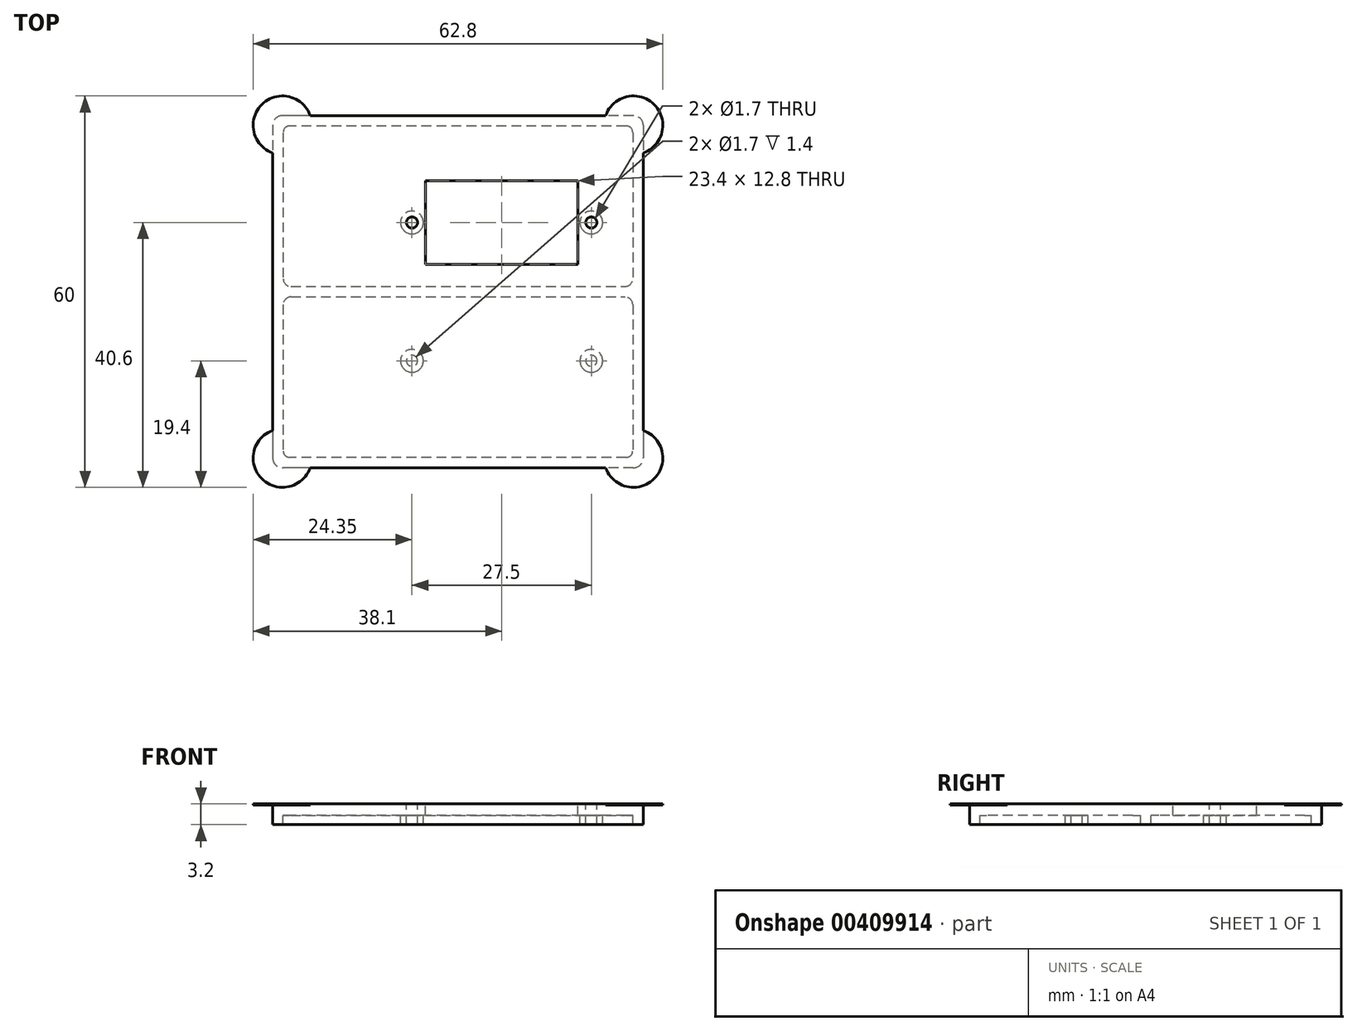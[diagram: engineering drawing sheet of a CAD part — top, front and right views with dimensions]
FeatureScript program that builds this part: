
annotation { "Feature Type Name" : "Feature", "Feature Type Description" : "" }
export const myFeature = defineFeature(function(context is Context, id is Id, definition is map)
    precondition{}
    {
        {
            var Q0;
            Q0=qCreatedBy(makeId("Top.planeOp"),FACE);
            var sketch = newSketch(context, id + "F0", { "sketchPlane" : qUnion([Q0])});
            skLineSegment(sketch, "E0.bottom", {"start": v(28.4, 27) * mm, "end": v(-28.4, 27) * mm});
            skLineSegment(sketch, "E0.top", {"start": v(28.4, -27) * mm, "end": v(-28.4, -27) * mm});
            skLineSegment(sketch, "E0.left", {"start": v(28.4, 27) * mm, "end": v(28.4, -27) * mm});
            skLineSegment(sketch, "E0.right", {"start": v(-28.4, 27) * mm, "end": v(-28.4, -27) * mm});
            skPoint(sketch, "E0.middle", {"position": v(0, 0) * mm});
            skCircle(sketch, "E1", {"center": v(-17.5, 14) * mm, "radius": 1.35 * mm, "construction": true});
            skCircle(sketch, "E2", {"center": v(-17.5, -14) * mm, "radius": 1.35 * mm, "construction": true});
            skCircle(sketch, "E3", {"center": v(17.5, 14) * mm, "radius": 1.35 * mm, "construction": true});
            skCircle(sketch, "E4", {"center": v(17.5, -14) * mm, "radius": 1.35 * mm, "construction": true});
            skLineSegment(sketch, "E5.bottom", {"start": v(-17.5, 14) * mm, "end": v(17.5, 14) * mm, "construction": true});
            skLineSegment(sketch, "E5.top", {"start": v(-17.5, -14) * mm, "end": v(17.5, -14) * mm, "construction": true});
            skLineSegment(sketch, "E5.left", {"start": v(-17.5, 14) * mm, "end": v(-17.5, -14) * mm, "construction": true});
            skLineSegment(sketch, "E5.right", {"start": v(17.5, 14) * mm, "end": v(17.5, -14) * mm, "construction": true});
            skLineSegment(sketch, "E6", {"start": v(-17.5, 0) * mm, "end": v(0, 0) * mm, "construction": true});
            skLineSegment(sketch, "E7", {"start": v(0, 14) * mm, "end": v(0, 0) * mm, "construction": true});
            skSolve(sketch);
        }
        {
            var Q0;
            Q0=qSketchRegion(id+"F0",true);
            extrude(context, id + "F1", {"entities" : qUnion([Q0]), "depth" : 1.8 * mm});
        }
        {
            var Q0;
            Q0=makeQuery(id+"F1.opExtrude","CAP_FACE",FACE,{"disambiguationData":[OSD([sQuery(id+"F0.wireOp",EDGE,"E0.bottom"),sQuery(id+"F0.wireOp",EDGE,"E0.top"),sQuery(id+"F0.wireOp",EDGE,"E0.left"),sQuery(id+"F0.wireOp",EDGE,"E0.right")])],"isStart":false});
            var sketch = newSketch(context, id + "F2", { "sketchPlane" : qUnion([Q0])});
            skLineSegment(sketch, "E8.bottom", {"start": v(-5, 4.2) * mm, "end": v(18.4, 4.2) * mm});
            skLineSegment(sketch, "E8.top", {"start": v(-5, 17) * mm, "end": v(18.4, 17) * mm});
            skLineSegment(sketch, "E8.left", {"start": v(-5, 4.2) * mm, "end": v(-5, 17) * mm});
            skLineSegment(sketch, "E8.right", {"start": v(18.4, 4.2) * mm, "end": v(18.4, 17) * mm});
            skCircle(sketch, "E9", {"center": v(-7.05, 10.6) * mm, "radius": 0.85 * mm});
            skPoint(sketch, "E9.centerSnap0", {"position": v(-5, 10.6) * mm});
            skCircle(sketch, "E10", {"center": v(20.45, 10.6) * mm, "radius": 0.85 * mm});
            skPoint(sketch, "E10.centerSnap0", {"position": v(18.4, 10.6) * mm});
            skLineSegment(sketch, "E11", {"start": v(-7.05, 10.6) * mm, "end": v(-5, 10.6) * mm, "construction": true});
            skLineSegment(sketch, "E12", {"start": v(18.4, 10.6) * mm, "end": v(20.45, 10.6) * mm, "construction": true});
            skSolve(sketch);
        }
        {
            var Q0;
            Q0=qSketchRegion(id+"F2",true);
            extrude(context, id + "F3", {"entities" : qUnion([Q0]), "operationType" : NewBodyOperationType.REMOVE, "endBound" : BoundingType.THROUGH_ALL, "oppositeDirection" : true, "depth" : 25 * mm});
        }
        {
            var Q0;
            Q0=makeQuery(id+"F1.opExtrude","SWEPT_EDGE",EDGE,{"disambiguationData":[OSD([sQuery(id+"F0.wireOp",EDGE,"E0.bottom"),sQuery(id+"F0.wireOp",EDGE,"E0.left")])]});
            var Q1;
            Q1=makeQuery(id+"F1.opExtrude","SWEPT_EDGE",EDGE,{"disambiguationData":[OSD([sQuery(id+"F0.wireOp",EDGE,"E0.top"),sQuery(id+"F0.wireOp",EDGE,"E0.left")])]});
            var Q2;
            Q2=makeQuery(id+"F1.opExtrude","SWEPT_EDGE",EDGE,{"disambiguationData":[OSD([sQuery(id+"F0.wireOp",EDGE,"E0.top"),sQuery(id+"F0.wireOp",EDGE,"E0.right")])]});
            var Q3;
            Q3=makeQuery(id+"F1.opExtrude","SWEPT_EDGE",EDGE,{"disambiguationData":[OSD([sQuery(id+"F0.wireOp",EDGE,"E0.bottom"),sQuery(id+"F0.wireOp",EDGE,"E0.right")])]});
            fillet(context, id + "F4", {"entities" : qUnion([Q0, Q1, Q2, Q3]), "radius" : 1.5 * mm, "tangentPropagation" : true, "allowEdgeOverflow" : false});
        }
        {
            var Q0;
            Q0=makeQuery(id+"F1.opExtrude","CAP_FACE",FACE,{"disambiguationData":[OSD([sQuery(id+"F0.wireOp",EDGE,"E0.bottom"),sQuery(id+"F0.wireOp",EDGE,"E0.top"),sQuery(id+"F0.wireOp",EDGE,"E0.left"),sQuery(id+"F0.wireOp",EDGE,"E0.right"),sQuery(id+"F0.wireOp",EDGE,"E1"),sQuery(id+"F0.wireOp",EDGE,"E2"),sQuery(id+"F0.wireOp",EDGE,"E3"),sQuery(id+"F0.wireOp",EDGE,"E4")])],"isStart":true});
            var sketch = newSketch(context, id + "F5", { "sketchPlane" : qUnion([Q0])});
            skLineSegment(sketch, "E13.0", {"start": v(-28.4, -25.5) * mm, "end": v(-28.4, 25.5) * mm});
            skLineSegment(sketch, "E14.0", {"start": v(26.9, -27) * mm, "end": v(-26.9, -27) * mm});
            skArc(sketch, "E15.0", {"start": v(-28.4, -25.5) * mm, "mid": v(-27.96, -26.56) * mm, "end": v(-26.9, -27) * mm});
            skArc(sketch, "E16.0.0", {"start": v(26.9, -27) * mm, "mid": v(27.96, -26.56) * mm, "end": v(28.4, -25.5) * mm});
            skArc(sketch, "E16.0.2", {"start": v(26.9, -27) * mm, "mid": v(27.96, -26.56) * mm, "end": v(28.4, -25.5) * mm});
            skLineSegment(sketch, "E17.0", {"start": v(28.4, -25.5) * mm, "end": v(28.4, 25.5) * mm});
            skArc(sketch, "E18.0", {"start": v(28.4, 25.5) * mm, "mid": v(27.96, 26.56) * mm, "end": v(26.9, 27) * mm});
            skLineSegment(sketch, "E19.0", {"start": v(26.9, 27) * mm, "end": v(-26.9, 27) * mm});
            skArc(sketch, "E20.0", {"start": v(-26.9, 27) * mm, "mid": v(-27.96, 26.56) * mm, "end": v(-28.4, 25.5) * mm});
            skCircle(sketch, "E21.0", {"center": v(20.45, 10.6) * mm, "radius": 0.85 * mm});
            skCircle(sketch, "E22.0", {"center": v(20.45, -10.6) * mm, "radius": 0.85 * mm});
            skCircle(sketch, "E23.0", {"center": v(-7.05, 10.6) * mm, "radius": 0.85 * mm});
            skCircle(sketch, "E24.0", {"center": v(-7.05, -10.6) * mm, "radius": 0.85 * mm});
            skCircle(sketch, "E25", {"center": v(-7.05, 10.6) * mm, "radius": 1.75 * mm});
            skCircle(sketch, "E26", {"center": v(-7.05, -10.6) * mm, "radius": 1.75 * mm});
            skCircle(sketch, "E27", {"center": v(20.45, 10.6) * mm, "radius": 1.75 * mm});
            skCircle(sketch, "E28", {"center": v(20.45, -10.6) * mm, "radius": 1.75 * mm});
            skLineSegment(sketch, "E29.1", {"start": v(26.8, -24.4) * mm, "end": v(26.8, 24.4) * mm});
            skLineSegment(sketch, "E29.2", {"start": v(25.8, 25.4) * mm, "end": v(-25.8, 25.4) * mm});
            skLineSegment(sketch, "E29.5", {"start": v(-26.8, -24.4) * mm, "end": v(-26.8, 24.4) * mm});
            skLineSegment(sketch, "E29.7", {"start": v(25.8, -25.4) * mm, "end": v(-25.8, -25.4) * mm});
            skLineSegment(sketch, "E30", {"start": v(-25.6, -0.8) * mm, "end": v(25.6, -0.8) * mm});
            skLineSegment(sketch, "E31", {"start": v(-25.6, 0.8) * mm, "end": v(25.6, 0.8) * mm});
            skLineSegment(sketch, "E32", {"start": v(0, 0.8) * mm, "end": v(0, 0) * mm, "construction": true});
            skLineSegment(sketch, "E33", {"start": v(0, 0) * mm, "end": v(0, -0.8) * mm, "construction": true});
            skArc(sketch, "E34", {"start": v(-26.8, 2) * mm, "mid": v(-26.45, 1.15) * mm, "end": v(-25.6, 0.8) * mm});
            skArc(sketch, "E35", {"start": v(-25.6, -0.8) * mm, "mid": v(-26.45, -1.15) * mm, "end": v(-26.8, -2) * mm});
            skArc(sketch, "E36", {"start": v(26.8, -2) * mm, "mid": v(26.45, -1.15) * mm, "end": v(25.6, -0.8) * mm});
            skArc(sketch, "E37", {"start": v(25.6, 0.8) * mm, "mid": v(26.45, 1.15) * mm, "end": v(26.8, 2) * mm});
            skPoint(sketch, "E38.orphan", {"position": v(-26.8, -0.8) * mm});
            skPoint(sketch, "E39.orphan", {"position": v(-26.8, 0.8) * mm});
            skPoint(sketch, "E40.orphan", {"position": v(26.8, 0.8) * mm});
            skPoint(sketch, "E41.orphan", {"position": v(26.8, -0.8) * mm});
            skArc(sketch, "E42.filletArc", {"start": v(25.8, -25.4) * mm, "mid": v(26.5, -25.1) * mm, "end": v(26.8, -24.4) * mm});
            skArc(sketch, "E43.filletArc", {"start": v(26.8, 24.4) * mm, "mid": v(26.5, 25.1) * mm, "end": v(25.8, 25.4) * mm});
            skArc(sketch, "E44.filletArc", {"start": v(-25.8, 25.4) * mm, "mid": v(-26.5, 25.1) * mm, "end": v(-26.8, 24.4) * mm});
            skArc(sketch, "E45.filletArc", {"start": v(-26.8, -24.4) * mm, "mid": v(-26.5, -25.1) * mm, "end": v(-25.8, -25.4) * mm});
            skSolve(sketch);
        }
        {
            var Q0;
            Q0=makeQuery(id+"F5.imprint","IMPRINT",FACE,{"disambiguationData":[TD([[makeQuery(id+"F5.imprint","IMPRINT",EDGE,{"derivedFrom":sQuery(id+"F5.wireOp",EDGE,"E23.0")}),-1.0]])]});
            var Q1;
            Q1=makeQuery(id+"F5.imprint","IMPRINT",FACE,{"disambiguationData":[TD([[makeQuery(id+"F5.imprint","IMPRINT",EDGE,{"derivedFrom":sQuery(id+"F5.wireOp",EDGE,"E24.0")}),1.0]])]});
            var Q2;
            Q2=makeQuery(id+"F5.imprint","IMPRINT",FACE,{"disambiguationData":[TD([[makeQuery(id+"F5.imprint","IMPRINT",EDGE,{"derivedFrom":sQuery(id+"F5.wireOp",EDGE,"E13.0")}),-1.0]])]});
            var Q3;
            Q3=makeQuery(id+"F5.imprint","IMPRINT",FACE,{"disambiguationData":[TD([[makeQuery(id+"F5.imprint","IMPRINT",EDGE,{"derivedFrom":sQuery(id+"F5.wireOp",EDGE,"E21.0")}),-1.0]])]});
            var Q4;
            Q4=makeQuery(id+"F5.imprint","IMPRINT",FACE,{"disambiguationData":[TD([[makeQuery(id+"F5.imprint","IMPRINT",EDGE,{"derivedFrom":sQuery(id+"F5.wireOp",EDGE,"E22.0")}),1.0]])]});
            var Q5;
            Q5=makeQuery(id+"F5.imprint","IMPRINT",FACE,{"disambiguationData":[TD([[makeQuery(id+"F5.imprint","IMPRINT",EDGE,{"derivedFrom":sQuery(id+"F5.wireOp",EDGE,"E30")}),1.0]])]});
            extrude(context, id + "F6", {"entities" : qUnion([Q0, Q1, Q2, Q3, Q4, Q5]), "operationType" : NewBodyOperationType.ADD, "depth" : 1.4 * mm});
        }
        {
            var Q0;
            Q0=makeQuery(id+"F1.opExtrude","CAP_FACE",FACE,{"disambiguationData":[OSD([sQuery(id+"F0.wireOp",EDGE,"E0.bottom"),sQuery(id+"F0.wireOp",EDGE,"E0.top"),sQuery(id+"F0.wireOp",EDGE,"E0.left"),sQuery(id+"F0.wireOp",EDGE,"E0.right")])],"isStart":false});
            var sketch = newSketch(context, id + "F7", { "sketchPlane" : qUnion([Q0])});
            skCircle(sketch, "E46", {"center": v(-26.9, 25.5) * mm, "radius": 4.5 * mm});
            skCircle(sketch, "E47", {"center": v(-26.9, -25.5) * mm, "radius": 4.5 * mm});
            skCircle(sketch, "E48", {"center": v(26.9, -25.5) * mm, "radius": 4.5 * mm});
            skCircle(sketch, "E49", {"center": v(26.9, 25.5) * mm, "radius": 4.5 * mm});
            skSolve(sketch);
        }
        {
            var Q0;
            Q0=qSketchRegion(id+"F7",true);
            extrude(context, id + "F8", {"entities" : qUnion([Q0]), "operationType" : NewBodyOperationType.ADD, "oppositeDirection" : true, "depth" : 0.2 * mm});
        }
    });
